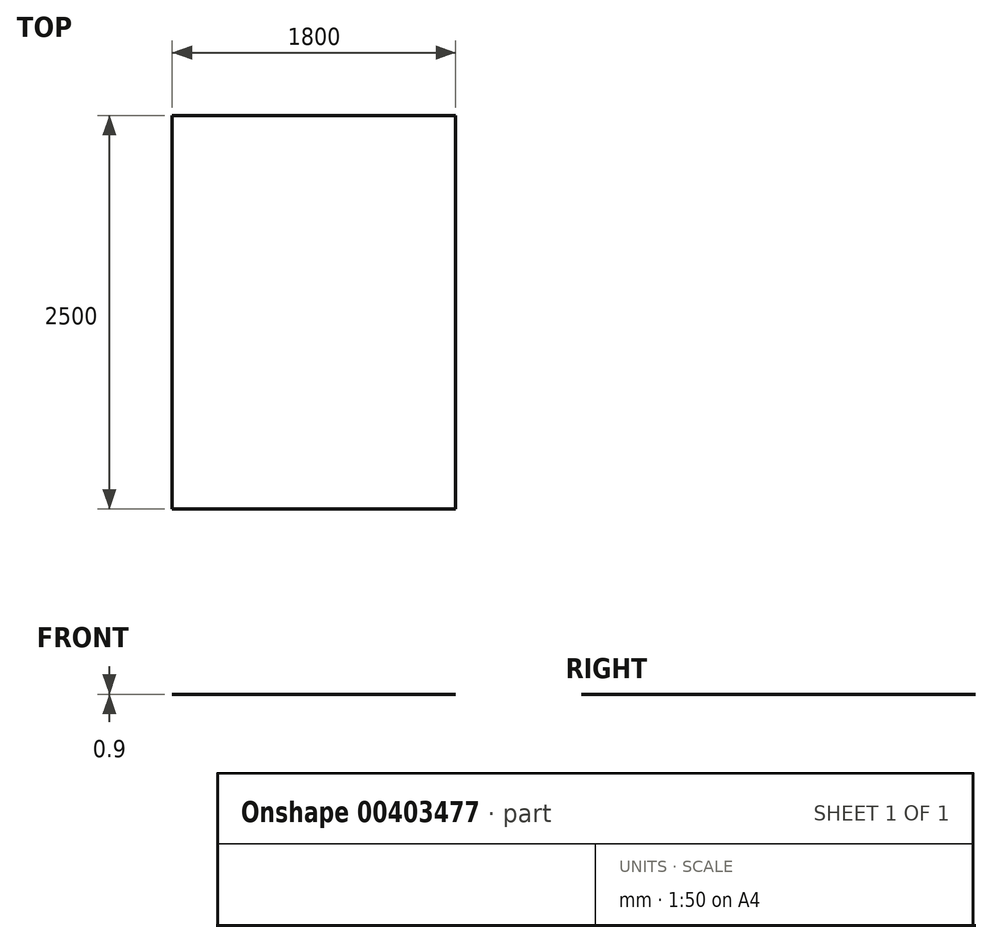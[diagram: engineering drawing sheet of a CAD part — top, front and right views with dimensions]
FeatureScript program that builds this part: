
annotation { "Feature Type Name" : "Feature", "Feature Type Description" : "" }
export const myFeature = defineFeature(function(context is Context, id is Id, definition is map)
    precondition{}
    {
        {
            var Q0;
            Q0=qCreatedBy(makeId("Top.planeOp"),FACE);
            var sketch = newSketch(context, id + "F0", { "sketchPlane" : qUnion([Q0])});
            skLineSegment(sketch, "E0.bottom", {"start": v(900, -1250) * mm, "end": v(-900, -1250) * mm});
            skLineSegment(sketch, "E0.top", {"start": v(900, 1250) * mm, "end": v(-900, 1250) * mm});
            skLineSegment(sketch, "E0.left", {"start": v(900, -1250) * mm, "end": v(900, 1250) * mm});
            skLineSegment(sketch, "E0.right", {"start": v(-900, -1250) * mm, "end": v(-900, 1250) * mm});
            skPoint(sketch, "E0.middle", {"position": v(0, 0) * mm});
            skSolve(sketch);
        }
        {
            var Q0;
            Q0=qSketchRegion(id+"F0",true);
            extrude(context, id + "F1", {"entities" : qUnion([Q0]), "depth" : 0.9 * mm});
        }
    });
